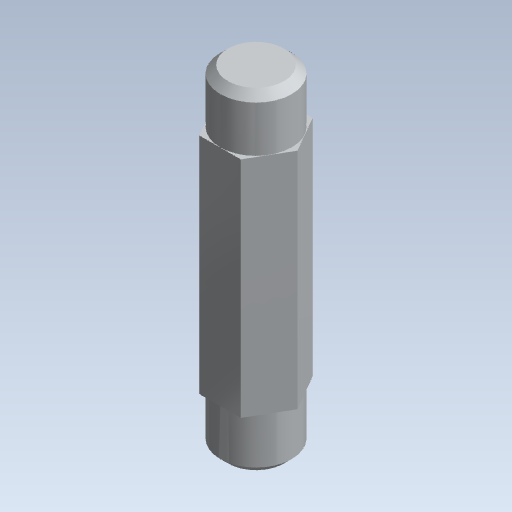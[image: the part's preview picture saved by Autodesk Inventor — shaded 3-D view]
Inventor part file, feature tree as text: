
AUTODESK INVENTOR PART (.ipt)
format: ipt  version: 2020 (Build 240168000, 168)  size: 72,704 bytes
history: native  units: mm (DEFAULTED — no unit token found)
features: chamfer x1
ambient origin geometry x8: Origin, YZ Plane, XZ Plane, XY Plane, X Axis, Y Axis, Z Axis, Center Point
bodies: Solid1 (feature_tree)
feature tree (1):
  chamfer  "Chamfer1"  [1 undecoded]
note: 1 required parameter value undecoded (feature->parameter linkage not recoverable at this tier; creation-order binding heuristic only, values carry confidence <= 0.55)
